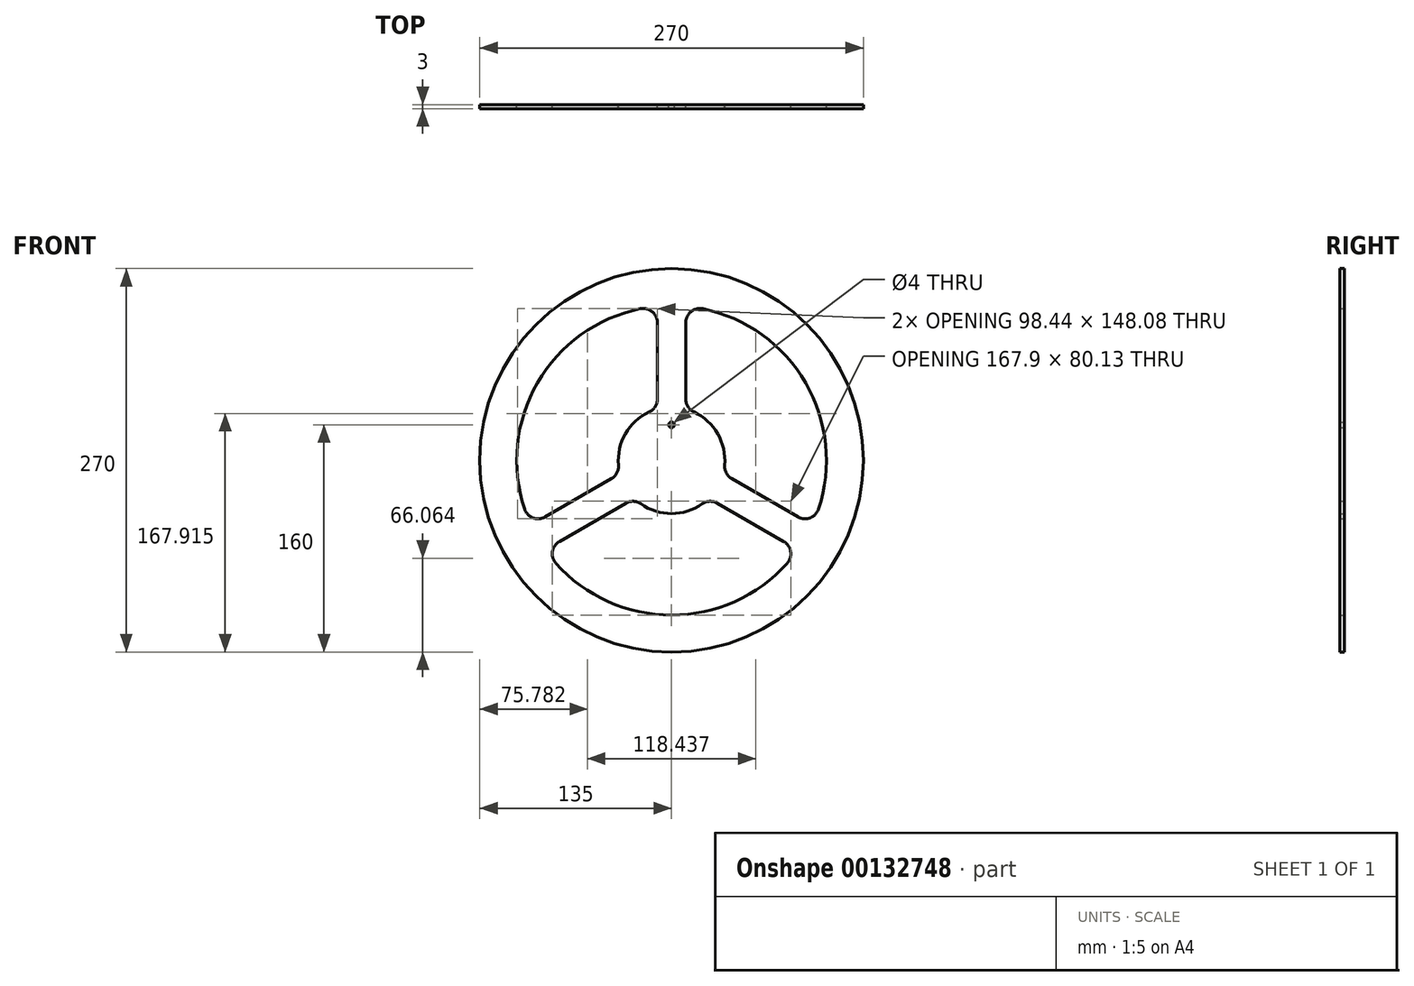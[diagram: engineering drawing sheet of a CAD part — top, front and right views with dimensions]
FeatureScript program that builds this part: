
annotation { "Feature Type Name" : "Feature", "Feature Type Description" : "" }
export const myFeature = defineFeature(function(context is Context, id is Id, definition is map)
    precondition{}
    {
        {
            var Q0;
            Q0=qCreatedBy(makeId("Front.planeOp"),FACE);
            var sketch = newSketch(context, id + "F0", { "sketchPlane" : qUnion([Q0])});
            skCircle(sketch, "E0", {"center": v(0, 0) * mm, "radius": 135 * mm});
            skArc(sketch, "E1", {"start": v(-15.79, 34.01) * mm, "mid": v(-32.48, 18.75) * mm, "end": v(-37.35, -3.33) * mm});
            skArc(sketch, "E2", {"start": v(-22.02, 106.75) * mm, "mid": v(-94.4, 54.5) * mm, "end": v(-103.46, -34.3) * mm});
            skLineSegment(sketch, "E3", {"start": v(-10, 43.08) * mm, "end": v(-10, 96.96) * mm});
            skLineSegment(sketch, "E4", {"start": v(10, 43.08) * mm, "end": v(10, 96.96) * mm});
            skLineSegment(sketch, "E5.1.0", {"start": v(-32.31, -30.2) * mm, "end": v(-78.97, -57.14) * mm});
            skLineSegment(sketch, "E5.1.1", {"start": v(-42.31, -12.88) * mm, "end": v(-88.97, -39.82) * mm});
            skLineSegment(sketch, "E5.2.0", {"start": v(42.31, -12.88) * mm, "end": v(88.97, -39.82) * mm});
            skLineSegment(sketch, "E5.2.1", {"start": v(32.31, -30.2) * mm, "end": v(78.97, -57.14) * mm});
            skArc(sketch, "E6.trimOffspring", {"start": v(103.46, -34.3) * mm, "mid": v(94.4, 54.5) * mm, "end": v(22.02, 106.75) * mm});
            skArc(sketch, "E7.trimOffspring", {"start": v(-21.56, -30.68) * mm, "mid": v(0, -37.5) * mm, "end": v(21.56, -30.68) * mm});
            skArc(sketch, "E8.trimOffspring", {"start": v(-81.44, -72.45) * mm, "mid": v(0, -109) * mm, "end": v(81.44, -72.45) * mm});
            skPoint(sketch, "E9.visualSharp", {"position": v(-99, -45.6) * mm});
            skArc(sketch, "E9.filletArc", {"start": v(-103.46, -34.3) * mm, "mid": v(-97.52, -40.5) * mm, "end": v(-88.97, -39.82) * mm});
            skPoint(sketch, "E10.visualSharp", {"position": v(-89, -62.93) * mm});
            skArc(sketch, "E10.filletArc", {"start": v(-78.97, -57.14) * mm, "mid": v(-83.84, -64.2) * mm, "end": v(-81.44, -72.45) * mm});
            skPoint(sketch, "E11.visualSharp", {"position": v(89, -62.93) * mm});
            skArc(sketch, "E11.filletArc", {"start": v(81.44, -72.45) * mm, "mid": v(83.84, -64.2) * mm, "end": v(78.97, -57.14) * mm});
            skArc(sketch, "E12.trimOffspring", {"start": v(37.35, -3.33) * mm, "mid": v(32.48, 18.75) * mm, "end": v(15.79, 34.01) * mm});
            skPoint(sketch, "E13.visualSharp", {"position": v(99, -45.6) * mm});
            skArc(sketch, "E13.filletArc", {"start": v(88.97, -39.82) * mm, "mid": v(97.52, -40.5) * mm, "end": v(103.46, -34.3) * mm});
            skPoint(sketch, "E14.visualSharp", {"position": v(10, 108.54) * mm});
            skArc(sketch, "E14.filletArc", {"start": v(22.02, 106.75) * mm, "mid": v(13.68, 104.71) * mm, "end": v(10, 96.96) * mm});
            skPoint(sketch, "E15.visualSharp", {"position": v(-10, 108.54) * mm});
            skArc(sketch, "E15.filletArc", {"start": v(-10, 96.96) * mm, "mid": v(-13.68, 104.71) * mm, "end": v(-22.02, 106.75) * mm});
            skPoint(sketch, "E16.visualSharp", {"position": v(36.3, -9.41) * mm});
            skArc(sketch, "E16.filletArc", {"start": v(37.35, -3.33) * mm, "mid": v(38.44, -8.83) * mm, "end": v(42.31, -12.88) * mm});
            skPoint(sketch, "E17.visualSharp", {"position": v(26.3, -26.73) * mm});
            skArc(sketch, "E17.filletArc", {"start": v(32.31, -30.2) * mm, "mid": v(26.87, -28.87) * mm, "end": v(21.56, -30.68) * mm});
            skPoint(sketch, "E18.visualSharp", {"position": v(-26.3, -26.73) * mm});
            skArc(sketch, "E18.filletArc", {"start": v(-21.56, -30.68) * mm, "mid": v(-26.87, -28.87) * mm, "end": v(-32.31, -30.2) * mm});
            skPoint(sketch, "E19.visualSharp", {"position": v(-36.3, -9.41) * mm});
            skArc(sketch, "E19.filletArc", {"start": v(-42.31, -12.88) * mm, "mid": v(-38.44, -8.83) * mm, "end": v(-37.35, -3.33) * mm});
            skPoint(sketch, "E20.visualSharp", {"position": v(-10, 36.14) * mm});
            skArc(sketch, "E20.filletArc", {"start": v(-15.79, 34.01) * mm, "mid": v(-11.57, 37.7) * mm, "end": v(-10, 43.08) * mm});
            skPoint(sketch, "E21.visualSharp", {"position": v(10, 36.14) * mm});
            skArc(sketch, "E21.filletArc", {"start": v(10, 43.08) * mm, "mid": v(11.57, 37.7) * mm, "end": v(15.79, 34.01) * mm});
            skSolve(sketch);
        }
        {
            var Q0;
            Q0 = qSketchRegion(id + "F0", true);
            extrude(context, id + "F1", {"entities" : qUnion([Q0]), "depth" : 3 * mm});
        }
        {
            var Q0;
            Q0=qCreatedBy(makeId("Front.planeOp"),FACE);
            var sketch = newSketch(context, id + "F2", { "sketchPlane" : qUnion([Q0])});
            skCircle(sketch, "E22", {"center": v(0, 25) * mm, "radius": 2 * mm});
            skSolve(sketch);
        }
        {
            var Q0;
            Q0=sQuery(id+"F2.wireOp",VERTEX,"E22.center");
            var Q1;
            Q1=makeQuery(id+"F1.opExtrude","SWEPT_BODY",BODY,{"disambiguationData":[OSD([sQuery(id+"F0.wireOp",EDGE,"E0"),sQuery(id+"F0.wireOp",EDGE,"E1"),sQuery(id+"F0.wireOp",EDGE,"E2"),sQuery(id+"F0.wireOp",EDGE,"E3"),sQuery(id+"F0.wireOp",EDGE,"E4"),sQuery(id+"F0.wireOp",EDGE,"E5.1.0"),sQuery(id+"F0.wireOp",EDGE,"E5.1.1"),sQuery(id+"F0.wireOp",EDGE,"E5.2.0"),sQuery(id+"F0.wireOp",EDGE,"E5.2.1"),sQuery(id+"F0.wireOp",EDGE,"E6.trimOffspring"),sQuery(id+"F0.wireOp",EDGE,"E7.trimOffspring"),sQuery(id+"F0.wireOp",EDGE,"E8.trimOffspring"),sQuery(id+"F0.wireOp",EDGE,"E9.filletArc"),sQuery(id+"F0.wireOp",EDGE,"E10.filletArc"),sQuery(id+"F0.wireOp",EDGE,"E11.filletArc"),sQuery(id+"F0.wireOp",EDGE,"E12.trimOffspring"),sQuery(id+"F0.wireOp",EDGE,"E13.filletArc"),sQuery(id+"F0.wireOp",EDGE,"E14.filletArc"),sQuery(id+"F0.wireOp",EDGE,"E15.filletArc"),sQuery(id+"F0.wireOp",EDGE,"E16.filletArc"),sQuery(id+"F0.wireOp",EDGE,"E17.filletArc"),sQuery(id+"F0.wireOp",EDGE,"E18.filletArc"),sQuery(id+"F0.wireOp",EDGE,"E19.filletArc"),sQuery(id+"F0.wireOp",EDGE,"E20.filletArc"),sQuery(id+"F0.wireOp",EDGE,"E21.filletArc")])]});
            hole(context, id + "F3", {"style" : HoleStyle.SIMPLE, "endStyle" : HoleEndStyle.THROUGH, "oppositeDirection" : true, "holeDiameter" : 4 * mm, "locations" : qUnion([Q0]), "scope" : qUnion([Q1]), "isTappedThrough" : true});
        }
    });
